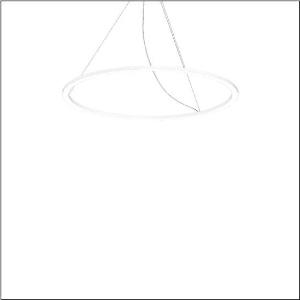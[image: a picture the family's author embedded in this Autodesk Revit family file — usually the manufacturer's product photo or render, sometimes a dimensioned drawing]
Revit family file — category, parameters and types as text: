
# Revit family: silica_r__21_ring-d_5pjbd3d3004a_4211
name_source: partatom
category: Lighting Fixtures
units: mm (PartAtom-declared; Revit-internal decimal feet)

## family parameters
Cut with Voids When Loaded = No
Host = Face
Light Source = No
Part Type = Normal
Room Calculation Point = No
Round Connector Dimension = Use Diameter
Shared = No

## types (1)
- Silica® 21 Ring-D (1 x LED, 8420 lm, 94 W, 4000K)
    Apparent Load = 94 VA
    CIE Flux Codes = 37 69 92 100 100
    Color Rendering = 80
    Color Temperature = 4000K
    Default Elevation = 1800 mm
    Description = Silica® 21 Ring-D, suspended luminaire, of PMMA, frosted, light emission: ring underside luminous distribution, primary light characteristic: symmetric, installation type: suspended mounting, LED, rated luminous flux: 8.420lm, luminous efficacy: 90lm/W, light colour: 840, colour temperature: 4000K, with terminal, 5-pole, mains connection: 230V, AC/DC, 0/50..60Hz, rated input power: 94W, housing, of extruded aluminium section, traffic white (RAL 9016), diameter: 1.100mm, ceiling canopy, traffic white (RAL 9016), protection rating (lamp compartment): IP40, insulation class (complete): insulation class I (protective earthing), certification: CE, impact resistance: IK02, permissible operating ambient temperature: 0..+35°C, packaging unit: 1 piece
    Height = 25 mm  [stored 0.082021 ft]
    Lamp = 1 x LED
    Lamp Light Flux = 8420 lm
    Lamp Power = 94 W
    Lamp count = 1
    Length = 1100 mm
    Luminous efficacy = 90 lm/W
    Manufacturer = Siteco
    ModVariant = No
    Model = 5PJBD3D3004A
    Mounting Place = Ceiling
    Mounting Type = Pendant
    Number of Poles = 1
    OnlyDefault = Yes
    Power Factor = 1
    Product Name = Silica® 21 Ring-D
    Product group = suspended luminaire
    ProductGroupID = 904
    Protection Class = Protection class I
    Protection Degree = Degree of protection
    RLX_Detail_Level = 1
    RLX_Emergency_Light_Flux = 0 lm
    RLX_Emergency_Type = 0
    RLX_Emergency_Type_DB = No
    RlxData = <blob elided: 12481 chars, md5=5f40cf30>
    Socket = socket
    Standby Power = 0 W
    System Light Flux = 8420 lm
    System Power = 94 W
    Type Comments = Product without accessories
    Type Image = l_1258355.jpg
    URL = http://relux.com
    VarID = ---
    Voltage = 0 V
    Weight = 0.00 kg
    Width = 0 mm  [stored 0 ft]

note: [stored X ft] marks values corroborated as IEEE doubles in the binary element streams (Revit-internal decimal feet)

## geometry (parser evidence)
native form markers: Sweep x9
no freeform markers — native parametric forms only
